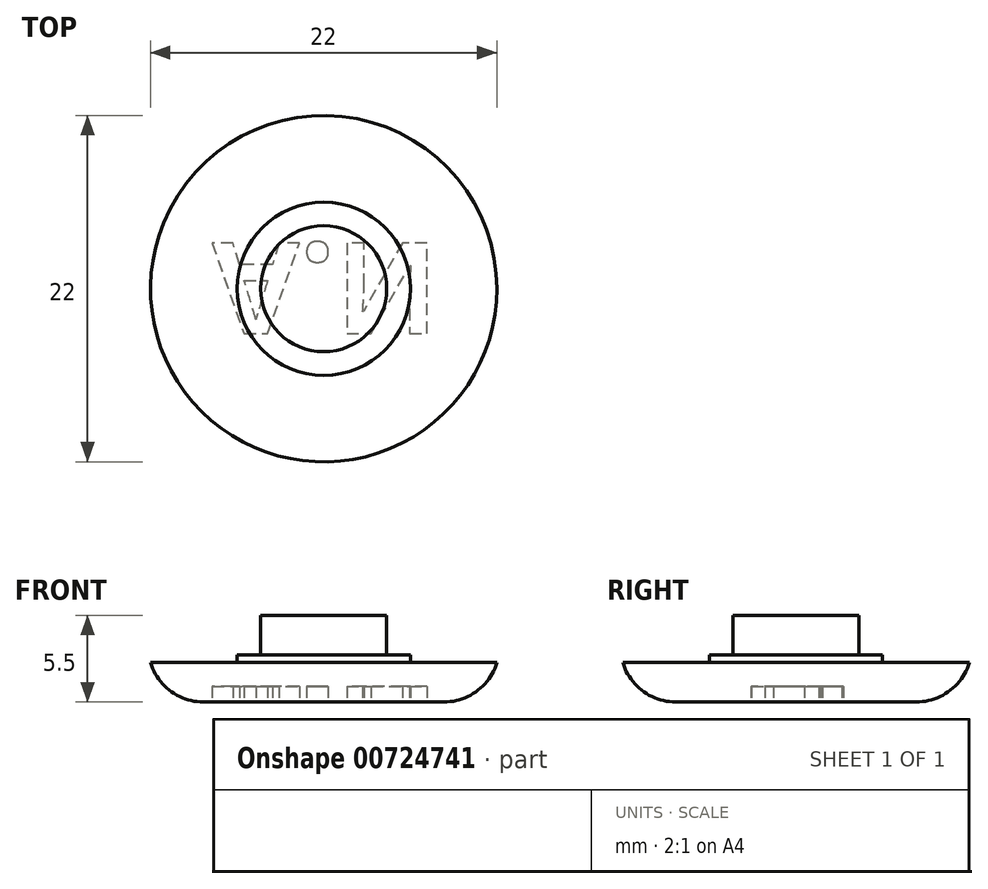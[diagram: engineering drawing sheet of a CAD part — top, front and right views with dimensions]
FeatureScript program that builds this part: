
annotation { "Feature Type Name" : "Feature", "Feature Type Description" : "" }
export const myFeature = defineFeature(function(context is Context, id is Id, definition is map)
    precondition{}
    {
        {
            var Q0;
            Q0=qCreatedBy(makeId("Top.planeOp"),FACE);
            var sketch = newSketch(context, id + "F0", { "sketchPlane" : qUnion([Q0])});
            skCircle(sketch, "E0", {"center": v(0, 0) * mm, "radius": 11 * mm});
            skCircle(sketch, "E1", {"center": v(0, 0) * mm, "radius": 4 * mm});
            skCircle(sketch, "E2", {"center": v(0, 0) * mm, "radius": 5.5 * mm});
            skSolve(sketch);
        }
        {
            var Q0;
            Q0=makeQuery(id+"F0.imprint","IMPRINT",FACE,{"disambiguationData":[TD([[makeQuery(id+"F0.imprint","IMPRINT",EDGE,{"derivedFrom":sQuery(id+"F0.wireOp",EDGE,"E0")}),1.0]])]});
            extrude(context, id + "F1", {"entities" : qUnion([Q0]), "depth" : 2.5 * mm, "offsetDistance" : 25 * mm});
        }
        {
            var Q0;
            Q0=makeQuery(id+"F0.imprint","IMPRINT",FACE,{"disambiguationData":[TD([[makeQuery(id+"F0.imprint","IMPRINT",EDGE,{"derivedFrom":sQuery(id+"F0.wireOp",EDGE,"E1")}),-1.0]])]});
            var Q1;
            Q1=makeQuery(id+"F1.opExtrude","CAP_FACE",FACE,{"disambiguationData":[OSD([sQuery(id+"F0.wireOp",EDGE,"E0"),sQuery(id+"F0.wireOp",EDGE,"E2")])],"isStart":false});
            extrude(context, id + "F2", {"entities" : qUnion([Q0]), "operationType" : NewBodyOperationType.ADD, "endBound" : BoundingType.UP_TO_SURFACE, "depth" : 25 * mm, "endBoundEntityFace" : qUnion([Q1]), "hasOffset" : true, "offsetDistance" : .5 * mm, "offsetOppositeDirection" : true});
        }
        {
            var Q0;
            Q0=makeQuery(id+"F0.imprint","IMPRINT",FACE,{"disambiguationData":[TD([[makeQuery(id+"F0.imprint","IMPRINT",EDGE,{"derivedFrom":sQuery(id+"F0.wireOp",EDGE,"E1")}),1.0]])]});
            var Q1;
            Q1=makeQuery(id+"F2.opExtrude","CAP_FACE",FACE,{"disambiguationData":[OSD([sQuery(id+"F0.wireOp",EDGE,"E0"),sQuery(id+"F0.wireOp",EDGE,"E2")])],"isStart":false});
            extrude(context, id + "F3", {"entities" : qUnion([Q0]), "operationType" : NewBodyOperationType.ADD, "endBound" : BoundingType.UP_TO_SURFACE, "depth" : 3 * mm, "endBoundEntityFace" : qUnion([Q1]), "hasOffset" : true, "offsetDistance" : 2.5 * mm, "offsetOppositeDirection" : true});
        }
        {
            var Q0;
            {var subQ0=sQuery(id+"F0.wireOp",EDGE,"E1");var subQ1=sQuery(id+"F0.wireOp",EDGE,"E2");Q0=makeQuery(id+"F3.boolean.opBoolean","MERGE",FACE,{"derivedFrom":[makeQuery(id+"F2.boolean.opBoolean","MERGE",FACE,{"derivedFrom":[makeQuery(id+"F1.opExtrude","CAP_FACE",FACE,{"disambiguationData":[OSD([sQuery(id+"F0.wireOp",EDGE,"E0"),subQ1])],"isStart":true}),makeQuery(id+"F2.opExtrude","CAP_FACE",FACE,{"disambiguationData":[OSD([subQ0,subQ1])],"isStart":true})]}),makeQuery(id+"F3.opExtrude","CAP_FACE",FACE,{"disambiguationData":[OSD([subQ0])],"isStart":true})]});}
            fillet(context, id + "F4", {"entities" : qUnion([Q0]), "radius" : 3.5 * mm, "tangentPropagation" : true, "allowEdgeOverflow" : false});
        }
        {
            var Q0;
            Q0=qCreatedBy(makeId("Right.planeOp"),FACE);
            var sketch = newSketch(context, id + "F5", { "sketchPlane" : qUnion([Q0])});
            skEllipse(sketch, "E3", {"center": v(-63.43, -1.89) * mm, "majorRadius": 11 * mm, "minorRadius": 2.5 * mm, "majorAxis": v(-1, 0)});
            skPoint(sketch, "E4", {"position": v(-63.43, 0.61) * mm});
            skLineSegment(sketch, "E5", {"start": v(-55.79, 0) * mm, "end": v(-71.08, 0) * mm});
            skArc(sketch, "E6", {"start": v(4.15, 3.3) * mm, "mid": v(11.14, 3.63) * mm, "end": v(4.15, 3.44) * mm});
            skArc(sketch, "E7", {"start": v(-11.15, 3.45) * mm, "mid": v(-11.14, 3.38) * mm, "end": v(-11.14, 3.3) * mm});
            skLineSegment(sketch, "E8", {"start": v(-63.43, 0.61) * mm, "end": v(-63.43, -4.39) * mm});
            skPoint(sketch, "E9.orphan", {"position": v(-63.43, -3.78) * mm});
            skPoint(sketch, "E10.orphan", {"position": v(-63.43, 0) * mm});
            skSolve(sketch);
        }
        {
            var Q0;
            {var subQ0=sQuery(id+"F0.wireOp",EDGE,"E1");var subQ1=sQuery(id+"F0.wireOp",EDGE,"E2");Q0=makeQuery(id+"F3.boolean.opBoolean","MERGE",FACE,{"derivedFrom":[makeQuery(id+"F2.boolean.opBoolean","MERGE",FACE,{"derivedFrom":[makeQuery(id+"F1.opExtrude","CAP_FACE",FACE,{"disambiguationData":[OSD([sQuery(id+"F0.wireOp",EDGE,"E0"),subQ1])],"isStart":true}),makeQuery(id+"F2.opExtrude","CAP_FACE",FACE,{"disambiguationData":[OSD([subQ0,subQ1])],"isStart":true})]}),makeQuery(id+"F3.opExtrude","CAP_FACE",FACE,{"disambiguationData":[OSD([subQ0])],"isStart":true})]});}
            var sketch = newSketch(context, id + "F6", { "sketchPlane" : qUnion([Q0])});
            skText(sketch, "E11", { "text": "A.N", "fontName": "OpenSans-Bold.ttf"});
            const initialGuessF6  = {"E11": [-0.00708, -0.0029, 1, 0, 0.00578]};
            skSetInitialGuess(sketch, initialGuessF6);
            skSolve(sketch);
        }
        {
            var Q0;
            Q0=qSketchRegion(id+"F6",true);
            extrude(context, id + "F7", {"entities" : qUnion([Q0]), "operationType" : NewBodyOperationType.REMOVE, "oppositeDirection" : true, "depth" : 1 * mm, "offsetDistance" : 25 * mm});
        }
    });
